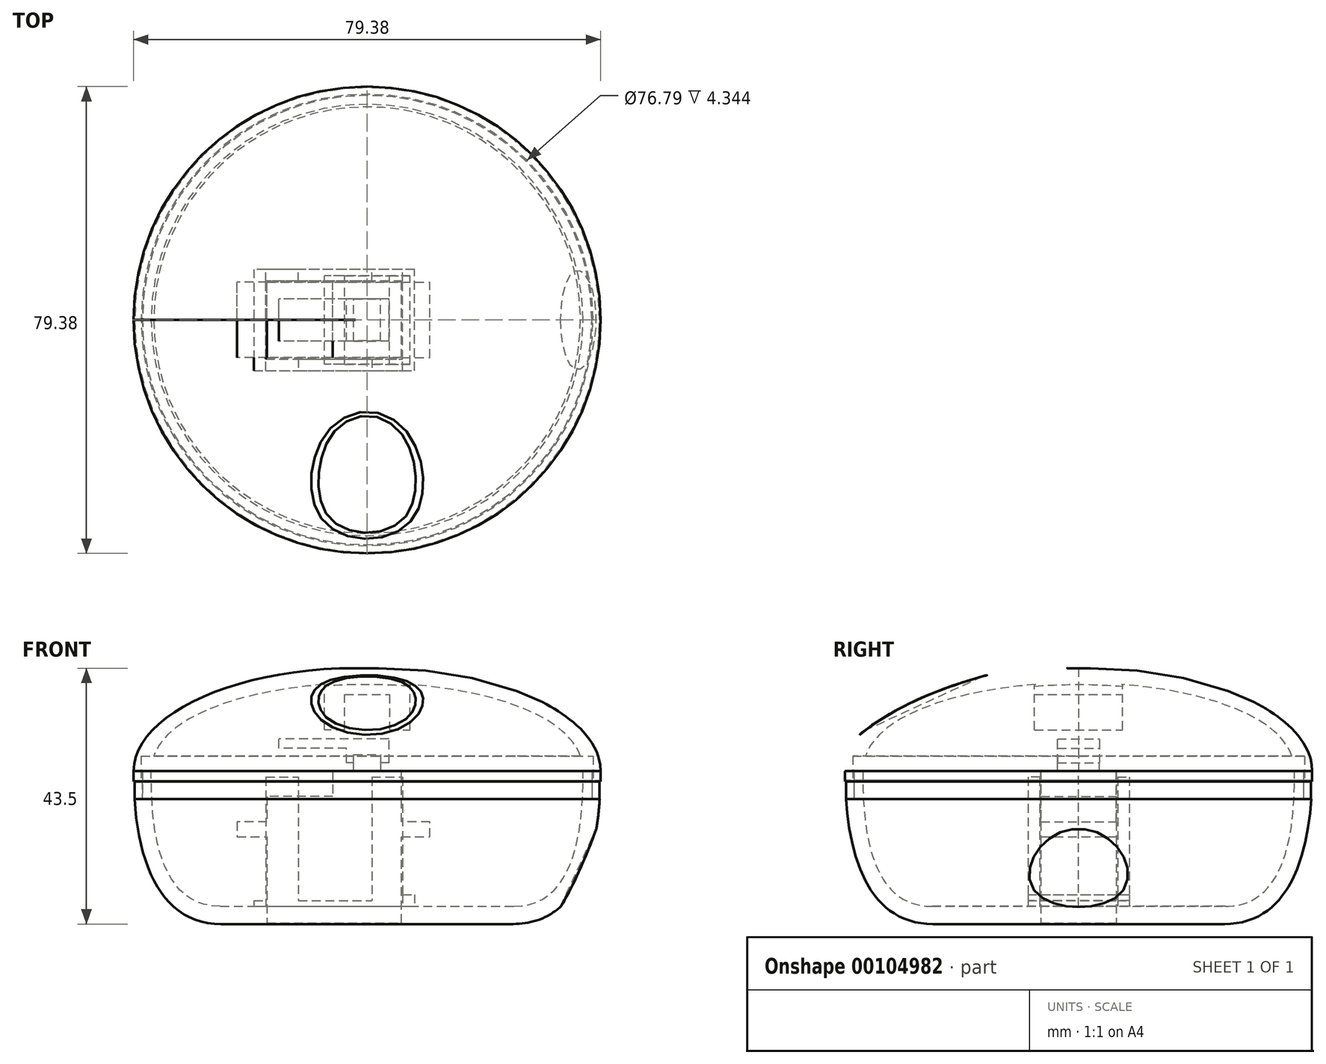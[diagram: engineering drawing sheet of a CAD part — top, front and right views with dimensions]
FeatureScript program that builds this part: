
annotation { "Feature Type Name" : "Feature", "Feature Type Description" : "" }
export const myFeature = defineFeature(function(context is Context, id is Id, definition is map)
    precondition{}
    {
        {
            var Q0;
            Q0=qCreatedBy(makeId("Front.planeOp"),FACE);
            var sketch = newSketch(context, id + "F0", { "sketchPlane" : qUnion([Q0])});
            skLineSegment(sketch, "E0", {"start": v(-62.74, 0) * mm, "end": v(62.74, 0) * mm, "construction": true});
            skLineSegment(sketch, "E1", {"start": v(0, -23) * mm, "end": v(24.93, -23) * mm});
            skFitSpline(sketch, "E2", {"points": [v(24.93, -23) * mm, v(36.69, 0) * mm], "startDerivative": vector(34.28, 0) * mm, "endDerivative": vector(0, 21.8) * mm});
            skLineSegment(sketch, "E3", {"start": v(0, -26) * mm, "end": v(24.8, -26) * mm});
            skFitSpline(sketch, "E4", {"points": [v(24.8, -26) * mm, v(39.69, 0) * mm], "startDerivative": vector(31.25, 0) * mm, "endDerivative": vector(0, 46.22) * mm});
            skLineSegment(sketch, "E5", {"start": v(0, -23) * mm, "end": v(0, -26) * mm});
            skLineSegment(sketch, "E6", {"start": v(36.69, 0) * mm, "end": v(39.69, 0) * mm});
            skLineSegment(sketch, "E7", {"start": v(38.19, 0) * mm, "end": v(38.19, -4.75) * mm});
            skLineSegment(sketch, "E8", {"start": v(38.19, -4.75) * mm, "end": v(39.54, -4.75) * mm});
            skPoint(sketch, "E9.oppositeSnap0", {"position": v(38.19, -2.38) * mm});
            skLineSegment(sketch, "E9.bottom", {"start": v(36.69, 0) * mm, "end": v(38.19, 0) * mm});
            skLineSegment(sketch, "E9.top", {"start": v(36.69, 1.57) * mm, "end": v(38.19, 1.57) * mm});
            skLineSegment(sketch, "E9.left", {"start": v(36.69, 0) * mm, "end": v(36.69, 1.57) * mm});
            skLineSegment(sketch, "E9.right", {"start": v(38.19, 0) * mm, "end": v(38.19, 1.57) * mm});
            skSolve(sketch);
        }
        {
            var Q0;
            Q0=qCreatedBy(makeId("Front.planeOp"),FACE);
            var sketch = newSketch(context, id + "F1", { "sketchPlane" : qUnion([Q0])});
            skLineSegment(sketch, "E10", {"start": v(-17.02, -25.82) * mm, "end": v(5.84, -25.82) * mm});
            skLineSegment(sketch, "E11", {"start": v(5.84, -25.82) * mm, "end": v(5.84, -11.18) * mm});
            skLineSegment(sketch, "E12", {"start": v(5.84, -11.18) * mm, "end": v(10.67, -11.18) * mm});
            skLineSegment(sketch, "E13", {"start": v(10.67, -11.18) * mm, "end": v(10.67, -8.64) * mm});
            skLineSegment(sketch, "E14", {"start": v(10.67, -8.64) * mm, "end": v(5.84, -8.64) * mm});
            skLineSegment(sketch, "E15", {"start": v(5.84, -8.64) * mm, "end": v(5.84, 0) * mm});
            skLineSegment(sketch, "E16", {"start": v(5.84, 0) * mm, "end": v(-5.84, 0) * mm});
            skLineSegment(sketch, "E17", {"start": v(-5.84, 0) * mm, "end": v(-5.84, -4.32) * mm});
            skLineSegment(sketch, "E18", {"start": v(-5.84, -4.32) * mm, "end": v(-17.02, -4.32) * mm});
            skLineSegment(sketch, "E19", {"start": v(-17.02, -4.32) * mm, "end": v(-17.02, -8.64) * mm});
            skLineSegment(sketch, "E20", {"start": v(-17.02, -8.64) * mm, "end": v(-22.1, -8.64) * mm});
            skLineSegment(sketch, "E21", {"start": v(-22.1, -8.64) * mm, "end": v(-22.1, -11.18) * mm});
            skLineSegment(sketch, "E22", {"start": v(-22.1, -11.18) * mm, "end": v(-17.02, -11.18) * mm});
            skLineSegment(sketch, "E23", {"start": v(-17.02, -11.18) * mm, "end": v(-17.02, -25.82) * mm});
            skPoint(sketch, "E24", {"position": v(0, 0) * mm});
            skLineSegment(sketch, "E25", {"start": v(-2.29, 0) * mm, "end": v(-2.29, 2.8) * mm});
            skLineSegment(sketch, "E26", {"start": v(-2.29, 2.8) * mm, "end": v(2.29, 2.8) * mm});
            skLineSegment(sketch, "E27", {"start": v(2.29, 2.8) * mm, "end": v(2.29, 0) * mm});
            skLineSegment(sketch, "E28", {"start": v(0, 0) * mm, "end": v(0, 24.97) * mm, "construction": true});
            skPoint(sketch, "E29.firstSnap0", {"position": v(2.29, 1.4) * mm});
            skLineSegment(sketch, "E29.bottom", {"start": v(3.73, 1.4) * mm, "end": v(-3.47, 1.4) * mm});
            skLineSegment(sketch, "E29.top", {"start": v(3.73, 3.88) * mm, "end": v(-3.47, 3.88) * mm});
            skLineSegment(sketch, "E29.left", {"start": v(3.73, 1.4) * mm, "end": v(3.73, 3.88) * mm});
            skLineSegment(sketch, "E29.right", {"start": v(-3.47, 1.4) * mm, "end": v(-3.47, 3.88) * mm});
            skLineSegment(sketch, "E30.bottom", {"start": v(3.73, 3.88) * mm, "end": v(-14.97, 3.88) * mm});
            skLineSegment(sketch, "E30.top", {"start": v(3.73, 5.48) * mm, "end": v(-14.97, 5.48) * mm});
            skLineSegment(sketch, "E30.left", {"start": v(3.73, 3.88) * mm, "end": v(3.73, 5.48) * mm});
            skLineSegment(sketch, "E30.right", {"start": v(-14.97, 3.88) * mm, "end": v(-14.97, 5.48) * mm});
            skSolve(sketch);
        }
        {
            var Q0;
            Q0=makeQuery(id+"F1.imprint","IMPRINT",FACE,{"disambiguationData":[TD([[makeQuery(id+"F1.imprint","IMPRINT",EDGE,{"derivedFrom":sQuery(id+"F1.wireOp",EDGE,"E10")}),1.0]])]});
            extrude(context, id + "F2", {"entities" : qUnion([Q0]), "endBound" : BoundingType.SYMMETRIC, "depth" : 12.83 * mm});
        }
        {
            var Q0;
            {var subQ0=sQuery(id+"F1.wireOp",EDGE,"E25");Q0=makeQuery(id+"F1.imprint","IMPRINT",FACE,{"disambiguationData":[TD([[makeQuery(id+"F1.imprint","IMPRINT",EDGE,{"derivedFrom":subQ0}),-1.0]])]});}
            extrude(context, id + "F3", {"entities" : qUnion([Q0]), "operationType" : NewBodyOperationType.ADD, "endBound" : BoundingType.SYMMETRIC, "depth" : 7.11 * mm});
        }
        {
            var Q0;
            Q0=makeQuery(id+"F0.imprint","IMPRINT",FACE,{"disambiguationData":[TD([[makeQuery(id+"F0.imprint","IMPRINT",EDGE,{"derivedFrom":sQuery(id+"F0.wireOp",EDGE,"E1")}),-1.0]])]});
            var Q1;
            Q1=makeQuery(id+"F0.imprint","IMPRINT",FACE,{"disambiguationData":[TD([[makeQuery(id+"F0.imprint","IMPRINT",EDGE,{"derivedFrom":sQuery(id+"F0.wireOp",EDGE,"E9.bottom")}),1.0]])]});
            var Q2;
            Q2=sQuery(id+"F1.wireOp",EDGE,"E28");
            revolve(context, id + "F4", {"entities" : qUnion([Q0, Q1]), "axis" : qUnion([Q2]), "revolveType" : RevolveType.FULL});
        }
        {
            var Q0;
            Q0=makeQuery(id+"F4.opRevolve","SWEPT_FACE",FACE,{"disambiguationData":[OSD([sQuery(id+"F0.wireOp",EDGE,"E1")])]});
            var sketch = newSketch(context, id + "F5", { "sketchPlane" : qUnion([Q0])});
            skLineSegment(sketch, "E31", {"start": v(-17.22, -6.61) * mm, "end": v(6.04, -6.61) * mm});
            skLineSegment(sketch, "E32", {"start": v(6.04, -6.61) * mm, "end": v(6.04, 6.61) * mm});
            skLineSegment(sketch, "E33", {"start": v(6.04, 6.61) * mm, "end": v(-17.22, 6.61) * mm});
            skLineSegment(sketch, "E34", {"start": v(-17.22, 6.61) * mm, "end": v(-17.22, -6.61) * mm});
            skLineSegment(sketch, "E35", {"start": v(8.04, 8.61) * mm, "end": v(-19.22, 8.61) * mm});
            skLineSegment(sketch, "E36", {"start": v(-19.22, 8.61) * mm, "end": v(-19.22, -8.61) * mm});
            skLineSegment(sketch, "E37", {"start": v(-19.22, -8.61) * mm, "end": v(8.04, -8.61) * mm});
            skLineSegment(sketch, "E38", {"start": v(8.04, -8.61) * mm, "end": v(8.04, 8.61) * mm});
            skLineSegment(sketch, "E39", {"start": v(-17.22, -6.61) * mm, "end": v(-17.22, -8.61) * mm});
            skLineSegment(sketch, "E40", {"start": v(-11.68, -6.61) * mm, "end": v(-11.68, -8.61) * mm});
            skLineSegment(sketch, "E41", {"start": v(6.04, -6.61) * mm, "end": v(6.04, -8.61) * mm});
            skLineSegment(sketch, "E42", {"start": v(0.8, -6.61) * mm, "end": v(0.8, -8.61) * mm});
            skLineSegment(sketch, "E43", {"start": v(6.04, -6.61) * mm, "end": v(8.04, -6.61) * mm});
            skLineSegment(sketch, "E44", {"start": v(6.04, 6.61) * mm, "end": v(8.04, 6.61) * mm});
            skLineSegment(sketch, "E45", {"start": v(-17.22, 6.61) * mm, "end": v(-17.22, 8.61) * mm});
            skLineSegment(sketch, "E46", {"start": v(-11.68, 6.61) * mm, "end": v(-11.68, 8.61) * mm});
            skPoint(sketch, "E46.startSnap0", {"position": v(-11.68, -7.61) * mm});
            skLineSegment(sketch, "E47", {"start": v(0.8, 6.61) * mm, "end": v(0.8, 8.61) * mm});
            skLineSegment(sketch, "E48", {"start": v(6.04, 6.61) * mm, "end": v(6.04, 8.61) * mm});
            skSolve(sketch);
        }
        {
            var Q0;
            {var subQ0=sQuery(id+"F5.wireOp",EDGE,"E39");Q0=makeQuery(id+"F5.imprint","IMPRINT",FACE,{"disambiguationData":[TD([[makeQuery(id+"F5.imprint","IMPRINT",EDGE,{"derivedFrom":subQ0}),1.0]])]});}
            var Q1;
            {var subQ0=sQuery(id+"F5.wireOp",EDGE,"E45");Q1=makeQuery(id+"F5.imprint","IMPRINT",FACE,{"disambiguationData":[TD([[makeQuery(id+"F5.imprint","IMPRINT",EDGE,{"derivedFrom":subQ0}),-1.0]])]});}
            var Q2;
            {var subQ2=sQuery(id+"F5.wireOp",EDGE,"E47");Q2=makeQuery(id+"F5.imprint","IMPRINT",FACE,{"disambiguationData":[TD([[makeQuery(id+"F5.imprint","IMPRINT",EDGE,{"derivedFrom":subQ2}),-1.0]])]});}
            var Q3;
            {var subQ0=sQuery(id+"F5.wireOp",EDGE,"E41");Q3=makeQuery(id+"F5.imprint","IMPRINT",FACE,{"disambiguationData":[TD([[makeQuery(id+"F5.imprint","IMPRINT",EDGE,{"derivedFrom":subQ0}),-1.0]])]});}
            var Q4;
            Q4=makeQuery(id+"F4.opRevolve","SWEPT_FACE",FACE,{"disambiguationData":[OSD([sQuery(id+"F0.wireOp",EDGE,"E6")])]});
            extrude(context, id + "F6", {"entities" : qUnion([Q0, Q1, Q2, Q3]), "operationType" : NewBodyOperationType.ADD, "endBoundEntityFace" : qUnion([Q4]), "depth" : 22 * mm});
        }
        {
            var Q0;
            Q0=qCreatedBy(makeId("Front.planeOp"),FACE);
            var sketch = newSketch(context, id + "F7", { "sketchPlane" : qUnion([Q0])});
            skLineSegment(sketch, "E49", {"start": v(0, 17.5) * mm, "end": v(1.98, 17.5) * mm});
            skLineSegment(sketch, "E50", {"start": v(0, 15) * mm, "end": v(0, 15) * mm});
            skLineSegment(sketch, "E51", {"start": v(0, 15) * mm, "end": v(0, 17.5) * mm});
            skFitSpline(sketch, "E52", {"points": [v(0, 15) * mm, v(36.69, 0) * mm], "startDerivative": vector(54.37, 0) * mm, "endDerivative": vector(0, -29.65) * mm});
            skFitSpline(sketch, "E53", {"points": [v(1.98, 17.5) * mm, v(39.69, 0) * mm], "startDerivative": vector(62.96, 0) * mm, "endDerivative": vector(0, -28.06) * mm});
            skLineSegment(sketch, "E54", {"start": v(24.8, 30.13) * mm, "end": v(24.8, -30.66) * mm, "construction": true});
            skLineSegment(sketch, "E55", {"start": v(36.69, 0) * mm, "end": v(39.69, 0) * mm});
            skLineSegment(sketch, "E56", {"start": v(38.4, 0) * mm, "end": v(38.4, -1.77) * mm});
            skLineSegment(sketch, "E57", {"start": v(38.4, -1.77) * mm, "end": v(39.69, -1.77) * mm});
            skLineSegment(sketch, "E58", {"start": v(39.69, -1.77) * mm, "end": v(39.69, 0) * mm});
            skLineSegment(sketch, "E59.bottom", {"start": v(38.4, 0) * mm, "end": v(35.84, 0) * mm});
            skLineSegment(sketch, "E59.top", {"start": v(38.4, 2.58) * mm, "end": v(35.84, 2.58) * mm});
            skLineSegment(sketch, "E59.left", {"start": v(38.4, 0) * mm, "end": v(38.4, 2.58) * mm});
            skLineSegment(sketch, "E59.right", {"start": v(35.84, 0) * mm, "end": v(35.84, 2.58) * mm});
            skSolve(sketch);
        }
        {
            var Q0;
            Q0=makeQuery(id+"F7.imprint","IMPRINT",FACE,{"disambiguationData":[TD([[makeQuery(id+"F7.imprint","IMPRINT",EDGE,{"derivedFrom":sQuery(id+"F7.wireOp",EDGE,"E55")}),-1.0]])]});
            var Q1;
            Q1=makeQuery(id+"F7.imprint","IMPRINT",FACE,{"disambiguationData":[TD([[makeQuery(id+"F7.imprint","IMPRINT",EDGE,{"derivedFrom":sQuery(id+"F7.wireOp",EDGE,"E49")}),-1.0]])]});
            var Q2;
            Q2=sQuery(id+"F1.wireOp",EDGE,"E28");
            revolve(context, id + "F8", {"entities" : qUnion([Q0, Q1]), "axis" : qUnion([Q2]), "revolveType" : RevolveType.FULL});
        }
        {
            var Q0;
            Q0=qCreatedBy(makeId("Front.planeOp"),FACE);
            var sketch = newSketch(context, id + "F9", { "sketchPlane" : qUnion([Q0])});
            skLineSegment(sketch, "E60", {"start": v(-3.8, 7.02) * mm, "end": v(-3.8, 13) * mm});
            skLineSegment(sketch, "E61", {"start": v(-3.8, 13) * mm, "end": v(3.81, 13) * mm});
            skLineSegment(sketch, "E62", {"start": v(3.81, 13) * mm, "end": v(3.81, 7.02) * mm});
            skLineSegment(sketch, "E63", {"start": v(3.81, 7.02) * mm, "end": v(7.27, 7.02) * mm});
            skLineSegment(sketch, "E64", {"start": v(7.27, 7.02) * mm, "end": v(7.27, 15.2) * mm});
            skLineSegment(sketch, "E65", {"start": v(-3.8, 7.02) * mm, "end": v(-7.27, 7.02) * mm});
            skLineSegment(sketch, "E66", {"start": v(-7.27, 7.02) * mm, "end": v(-7.27, 15.2) * mm});
            skLineSegment(sketch, "E67", {"start": v(-7.27, 15.2) * mm, "end": v(7.27, 15.2) * mm});
            skSolve(sketch);
        }
        {
            var Q0;
            Q0=makeQuery(id+"F9.imprint","IMPRINT",FACE,{"disambiguationData":[TD([[makeQuery(id+"F9.imprint","IMPRINT",EDGE,{"derivedFrom":sQuery(id+"F9.wireOp",EDGE,"E60")}),1.0]])]});
            extrude(context, id + "F10", {"entities" : qUnion([Q0]), "operationType" : NewBodyOperationType.ADD, "endBound" : BoundingType.SYMMETRIC, "depth" : 15 * mm});
        }
        {
            var Q0;
            Q0=makeQuery(id+"F5.imprint","IMPRINT",FACE,{"disambiguationData":[TD([[makeQuery(id+"F5.imprint","IMPRINT",EDGE,{"derivedFrom":sQuery(id+"F5.wireOp",EDGE,"E32")}),-1.0]])]});
            var Q1;
            {var subQ3=sQuery(id+"F5.wireOp",EDGE,"E41");Q1=makeQuery(id+"F5.imprint","IMPRINT",FACE,{"disambiguationData":[TD([[makeQuery(id+"F5.imprint","IMPRINT",EDGE,{"derivedFrom":subQ3}),1.0]])]});}
            var Q2;
            {var subQ4=sQuery(id+"F5.wireOp",EDGE,"E44");Q2=makeQuery(id+"F5.imprint","IMPRINT",FACE,{"disambiguationData":[TD([[makeQuery(id+"F5.imprint","IMPRINT",EDGE,{"derivedFrom":subQ4}),1.0]])]});}
            extrude(context, id + "F11", {"entities" : qUnion([Q0, Q1, Q2]), "operationType" : NewBodyOperationType.ADD, "depth" : 2 * mm});
        }
        {
            var Q0;
            {var subQ0=sQuery(id+"F5.wireOp",EDGE,"E40");Q0=makeQuery(id+"F5.imprint","IMPRINT",FACE,{"disambiguationData":[TD([[makeQuery(id+"F5.imprint","IMPRINT",EDGE,{"derivedFrom":subQ0}),1.0]])]});}
            var Q1;
            {var subQ0=sQuery(id+"F5.wireOp",EDGE,"E46");Q1=makeQuery(id+"F5.imprint","IMPRINT",FACE,{"disambiguationData":[TD([[makeQuery(id+"F5.imprint","IMPRINT",EDGE,{"derivedFrom":subQ0}),-1.0]])]});}
            var Q2;
            Q2=makeQuery(id+"F5.imprint","IMPRINT",FACE,{"disambiguationData":[TD([[makeQuery(id+"F5.imprint","IMPRINT",EDGE,{"derivedFrom":sQuery(id+"F5.wireOp",EDGE,"E34")}),-1.0]])]});
            extrude(context, id + "F12", {"entities" : qUnion([Q0, Q1, Q2]), "operationType" : NewBodyOperationType.ADD, "depth" : 1 * mm});
        }
        {
            var Q0;
            {var subQ4=sQuery(id+"F1.wireOp",EDGE,"E26");Q0=makeQuery(id+"F1.imprint","IMPRINT",FACE,{"disambiguationData":[TD([[makeQuery(id+"F1.imprint","IMPRINT",EDGE,{"derivedFrom":subQ4}),1.0]])]});}
            var Q1;
            Q1=makeQuery(id+"F1.imprint","IMPRINT",FACE,{"disambiguationData":[TD([[makeQuery(id+"F1.imprint","IMPRINT",EDGE,{"derivedFrom":sQuery(id+"F1.wireOp",EDGE,"E30.top")}),1.0]])]});
            extrude(context, id + "F13", {"entities" : qUnion([Q0, Q1]), "operationType" : NewBodyOperationType.ADD, "endBound" : BoundingType.SYMMETRIC, "depth" : 7.2 * mm});
        }
        {
            var Q0;
            Q0=qCreatedBy(makeId("Right.planeOp"),FACE);
            var sketch = newSketch(context, id + "F14", { "sketchPlane" : qUnion([Q0])});
            skLineSegment(sketch, "E68", {"start": v(-10.06, 21.96) * mm, "end": v(-51.03, 3.17) * mm});
            skSolve(sketch);
        }
        {
            var Q0;
            Q0=sQuery(id+"F14.wireOp",EDGE,"E68");
            var Q1;
            Q1=sQuery(id+"F14.wireOp",VERTEX,"E68.end");
            cPlane(context, id + "F15", {"entities" : qUnion([Q0, Q1]), "cplaneType" : CPlaneType.LINE_POINT, "offset" : 25 * mm, "width" : 150 * mm, "height" : 150 * mm});
        }
        {
            var Q0;
            Q0=qCreatedBy(id+"F15.planeOp",FACE);
            var sketch = newSketch(context, id + "F16", { "sketchPlane" : qUnion([Q0])});
            skEllipse(sketch, "E69", {"center": v(0, 24.15) * mm, "majorRadius": 11 * mm, "minorRadius": 2.75 * mm, "majorAxis": v(1, 0)});
            skSolve(sketch);
        }
        {
            var Q0;
            Q0=makeQuery(id+"F16.imprint","IMPRINT",FACE,{"disambiguationData":[TD([[makeQuery(id+"F16.imprint","IMPRINT",EDGE,{"derivedFrom":sQuery(id+"F16.wireOp",EDGE,"E69")}),1.0]])]});
            extrude(context, id + "F17", {"entities" : qUnion([Q0]), "operationType" : NewBodyOperationType.REMOVE, "oppositeDirection" : true, "depth" : 50 * mm});
        }
        {
            var Q0;
            Q0=makeQuery(id+"F17.boolean.opBoolean","INTERSECT",EDGE,{"derivedFrom":[makeQuery(id+"F8.opRevolve","SWEPT_FACE",FACE,{"disambiguationData":[OSD([sQuery(id+"F7.wireOp",EDGE,"E53")])]}),makeQuery(id+"F17.opExtrude","SWEPT_FACE",FACE,{"disambiguationData":[OSD([sQuery(id+"F16.wireOp",EDGE,"E69")])]})]});
            fillet(context, id + "F18", {"entities" : qUnion([Q0]), "radius" : 3 * mm, "tangentPropagation" : true, "allowEdgeOverflow" : false});
        }
        {
            var Q0;
            Q0=qCreatedBy(makeId("Front.planeOp"),FACE);
            var sketch = newSketch(context, id + "F19", { "sketchPlane" : qUnion([Q0])});
            skLineSegment(sketch, "E70.bottom", {"start": v(38.21, -1.58) * mm, "end": v(39.5, -1.58) * mm});
            skLineSegment(sketch, "E70.top", {"start": v(38.21, -4.75) * mm, "end": v(39.5, -4.75) * mm});
            skLineSegment(sketch, "E70.left", {"start": v(38.21, -1.58) * mm, "end": v(38.21, -4.75) * mm});
            skLineSegment(sketch, "E70.right", {"start": v(39.5, -1.58) * mm, "end": v(39.5, -4.75) * mm});
            skSolve(sketch);
        }
        {
            var Q0;
            Q0=makeQuery(id+"F19.imprint","IMPRINT",FACE,{"disambiguationData":[TD([[makeQuery(id+"F19.imprint","IMPRINT",EDGE,{"derivedFrom":sQuery(id+"F19.wireOp",EDGE,"E70.bottom")}),-1.0]])]});
            var Q1;
            Q1=sQuery(id+"F1.wireOp",EDGE,"E28");
            revolve(context, id + "F20", {"entities" : qUnion([Q0]), "axis" : qUnion([Q1]), "revolveType" : RevolveType.FULL});
        }
        {
            var Q0;
            Q0=qCreatedBy(makeId("Front.planeOp"),FACE);
            var sketch = newSketch(context, id + "F21", { "sketchPlane" : qUnion([Q0])});
            skLineSegment(sketch, "E71", {"start": v(33.97, -30.38) * mm, "end": v(47.86, -0.16) * mm});
            skSolve(sketch);
        }
        {
            var Q0;
            Q0=sQuery(id+"F21.wireOp",EDGE,"E71");
            var Q1;
            Q1=sQuery(id+"F21.wireOp",VERTEX,"E71.start");
            cPlane(context, id + "F22", {"entities" : qUnion([Q0, Q1]), "cplaneType" : CPlaneType.LINE_POINT, "offset" : 25 * mm, "width" : 150 * mm, "height" : 150 * mm});
        }
        {
            var Q0;
            Q0=qCreatedBy(id+"F22.planeOp",FACE);
            var sketch = newSketch(context, id + "F23", { "sketchPlane" : qUnion([Q0])});
            skEllipse(sketch, "E72", {"center": v(45.5, 0) * mm, "majorRadius": 25 * mm, "minorRadius": 6 * mm, "majorAxis": v(0, 1)});
            skSolve(sketch);
        }
        {
            var Q0;
            Q0=makeQuery(id+"F23.imprint","IMPRINT",FACE,{"disambiguationData":[TD([[makeQuery(id+"F23.imprint","IMPRINT",EDGE,{"derivedFrom":sQuery(id+"F23.wireOp",EDGE,"E72")}),1.0]])]});
            extrude(context, id + "F24", {"entities" : qUnion([Q0]), "operationType" : NewBodyOperationType.REMOVE, "depth" : 35 * mm});
        }
    });
